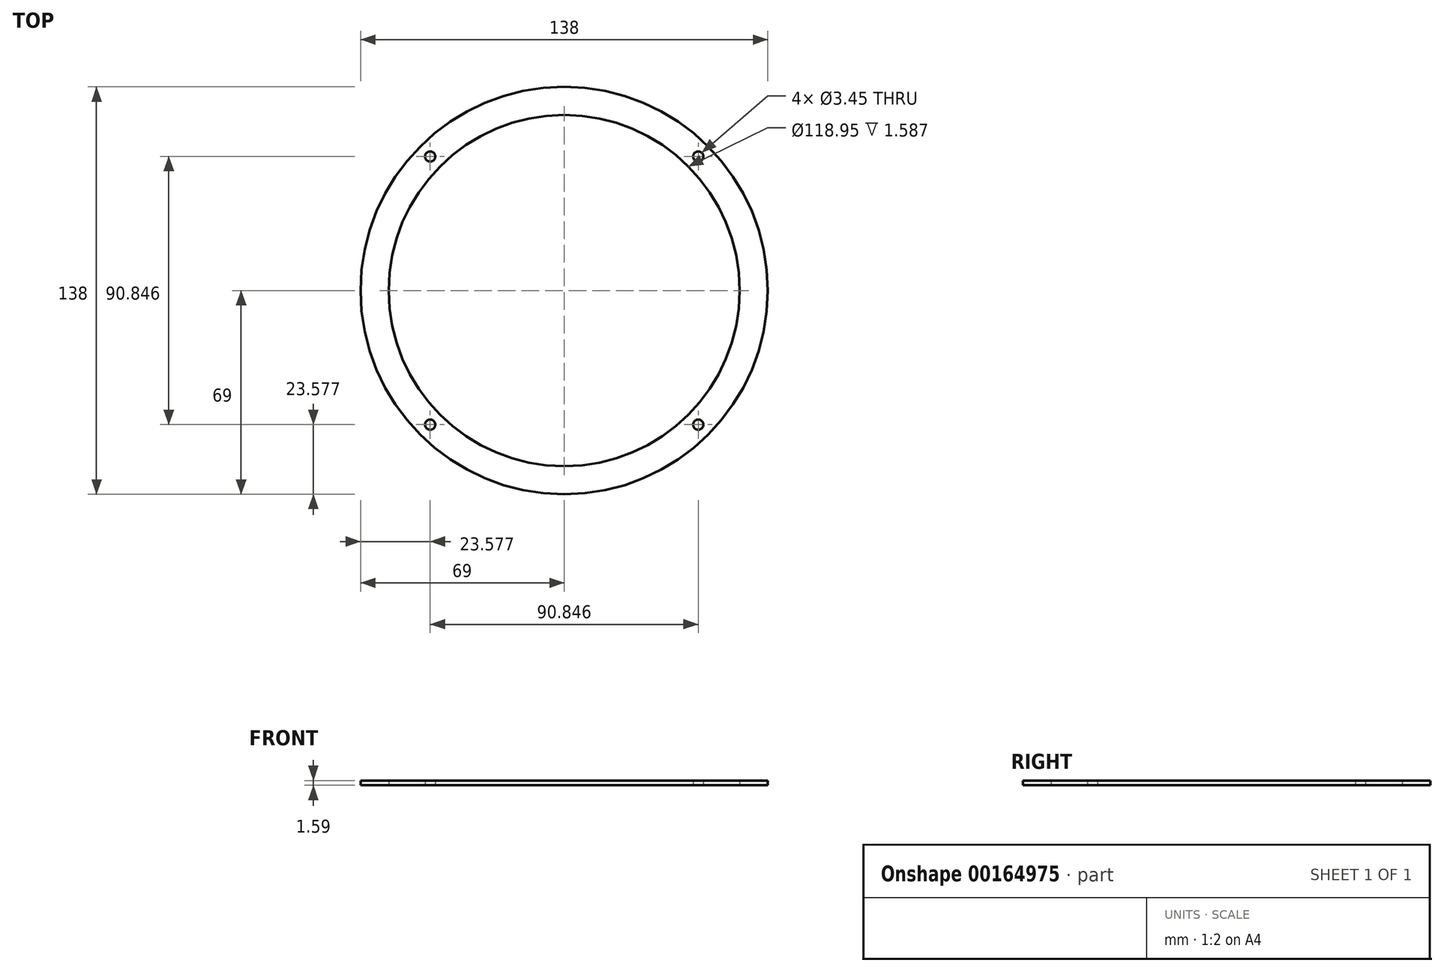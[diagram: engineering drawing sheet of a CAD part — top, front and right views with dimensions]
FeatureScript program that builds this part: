
annotation { "Feature Type Name" : "Feature", "Feature Type Description" : "" }
export const myFeature = defineFeature(function(context is Context, id is Id, definition is map)
    precondition{}
    {
        {
            var Q0;
            Q0=qCreatedBy(makeId("Top.planeOp"),FACE);
            var sketch = newSketch(context, id + "F0", { "sketchPlane" : qUnion([Q0])});
            skCircle(sketch, "E0", {"center": v(0, 0) * mm, "radius": 59.47 * mm});
            skCircle(sketch, "E1", {"center": v(0, 0) * mm, "radius": 69 * mm});
            skLineSegment(sketch, "E2.bottom", {"start": v(45.42, 45.42) * mm, "end": v(-45.42, 45.42) * mm, "construction": true});
            skLineSegment(sketch, "E2.top", {"start": v(45.42, -45.42) * mm, "end": v(-45.42, -45.42) * mm, "construction": true});
            skLineSegment(sketch, "E2.left", {"start": v(45.42, 45.42) * mm, "end": v(45.42, -45.42) * mm, "construction": true});
            skLineSegment(sketch, "E2.right", {"start": v(-45.42, 45.42) * mm, "end": v(-45.42, -45.42) * mm, "construction": true});
            skCircle(sketch, "E3", {"center": v(-45.42, 45.42) * mm, "radius": 4.76 * mm, "construction": true});
            skCircle(sketch, "E4", {"center": v(-45.42, 45.42) * mm, "radius": 1.73 * mm});
            skCircle(sketch, "E5", {"center": v(45.42, 45.42) * mm, "radius": 1.73 * mm});
            skCircle(sketch, "E6", {"center": v(45.42, -45.42) * mm, "radius": 1.73 * mm});
            skCircle(sketch, "E7", {"center": v(-45.42, -45.42) * mm, "radius": 1.73 * mm});
            skSolve(sketch);
        }
        {
            var Q0;
            Q0=qSketchRegion(id+"F0",true);
            extrude(context, id + "F1", {"entities" : qUnion([Q0]), "depth" : 1.59 * mm});
        }
    });
